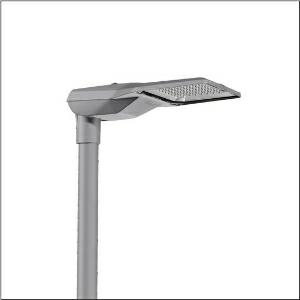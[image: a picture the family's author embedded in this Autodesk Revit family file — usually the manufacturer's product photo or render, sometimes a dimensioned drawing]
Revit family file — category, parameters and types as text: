
# Revit family: streetlight_sl_21_midi___p0_8a_5xe3u33s08lb_a919
name_source: partatom
category: Lighting Fixtures
units: mm (PartAtom-declared; Revit-internal decimal feet)

## family parameters
Cut with Voids When Loaded = No
Host = Face
Light Source = No
Part Type = Normal
Room Calculation Point = No
Round Connector Dimension = Use Diameter
Shared = No

## types (1)
- --- (1 x LED, 14470 lm, 99.6 W, 3000K)
    Apparent Load = 100 VA
    CIE Flux Codes = 33 69 96 100 100
    Color Rendering = 70
    Color Temperature = 3000K
    Default Elevation = 1800 mm
    Description = Streetlight SL 21 midi, mast luminaire, primary light control with lens, of PMMA, primary optical cover: cover, of toughened safety glass, transparent, light distribution: P0.8a, light emission: direct distribution, primary light characteristic: asymmetric, installation type: post-top, side-entry, LED, High Power LED, rated luminous flux: 14.470lm, luminous efficacy: 145lm/W, light colour: 730, colour temperature: 3000K, control gear: D4i, control: pre-setting: logarithmic dimming characteristic, flexible luminous flux parameterisation, time-dependent luminous flux control, constant luminous flux control, overheat protection, mains connection: 230..240V, AC, 50/60Hz, start of lifetime: 100W, end of service life: 102W, reduction: 46W, luminaire housing, of diecast aluminium, powder-coated, SITECO metallic grey (DB 702S), corrosivity category C5 high according to DIN EN ISO 12944, multi-level sealing system, sealing non-destructively replaceable, inclination adjustable: 0°, 5°, 10°, 15°, please order mast flange separately, length: 644mm, width: 335mm, height: 110mm, mast flange for spigot size: 42mm (side-entry): 5XC10008XM4, 60/48mm (side-entry/post-top): 5XC10108XM2, 76/60mm (side-entry/post-top): 5XC10108XM1, mounting height: 4..8m, Smart Interface above, protection rating (complete): IP66, insulation class (complete): insulation class II (safety insulation), certification: CE, ENEC, ENEC+, VDE, impact resistance: IK10, permissible operating ambient temperature for outdoor applications: -40..+50°C, standard-compliant lighting for roads and squares, packaging unit: 1 piece

Light Distribution: P0.8a
    Height = 111 mm
    Lamp = 1 x LED
    Lamp Light Flux = 14470 lm
    Lamp Power = 99.6 W
    Lamp count = 1
    Length = 644 mm
    Luminous efficacy = 145 lm/W
    Manufacturer = Siteco
    ModVariant = No
    Model = 5XE3U33S08LB
    Number of Poles = 1
    OnlyDefault = Yes
    Power Factor = 1
    Product Name = Streetlight SL 21 midi | P0.8a
    Product group = mast luminaire | pylon top
    ProductGroupID = 6100
    Protection Class = Protection class II
    Protection Degree = IP 66
    RLX_Detail_Level = 1
    RLX_Emergency_Light_Flux = 0 lm
    RLX_Emergency_Type = 0
    RLX_Emergency_Type_DB = No
    RlxData = <blob elided: 26613 chars, md5=cfff011e>
    Socket = socket
    Standby Power = 0 W
    System Light Flux = 14470 lm
    System Power = 100 W
    Type Comments = factory setting: luminous flux: 100 % | dim-lin: 254 | 1020 mA
    Type Image = l_1004302.jpg
    URL = http://relux.com
    VarID = @adj_033191
    Voltage = 0 V
    Weight = 0.00 kg
    Width = 336 mm

## geometry (parser evidence)
native form markers: Blend x4, Sweep x10
no freeform markers — native parametric forms only
